# Revit family: HansWeitzel_4133
name_source: partatom
category: Allgemeines Modell
revit_build: Autodesk Revit 2017 (Build: 20160225_1515(x64)
units: mm (PartAtom-declared; Revit-internal decimal feet)

## family parameters
Basisbauteil = Wand
Beim Laden mit Abzugskörper schneiden = Nein
Bemaßung runder Anschluss = Durchmesser verwenden
Gemeinsam genutzt = Nein
Immer vertikal = Ja
Kann Basisbauteil für Bewehrung sein = Nein
Raumberechnungspunkt = Nein
Teiletyp = Normal

## types (1)
- HansWeitzel_4133
    BIM = https://media.live.bim.site
    BIMSITE_PRODUCT_ID = 6ce841d8c003c2f0351888f5bd4c5b56915332c2
    Beschreibung = HZ-Stoßverbinder BLF Buche dunkel Formteil an Sollbruchstelle einkürzen
    Breite [mm] = 40
    Dekor = Buche dunkel
    Farbton = Holzart/Holzdekor
    GTIN = 4022023208719
    Gewicht unverpackt (netto) [kg] = 0.008
    HAN = 4133
    HeinzeBIM = https://www.heinze.de
    Hersteller = Hans Weitzel GmbH & Co. KG
    Höhe [mm] = 93
    Ist System = Nein
    Ist Zubehör = Nein
    Menge pro Verpackungseinheit = 10
    Profilart = Anschlussprofi
    Tiefe (mm) = 30
    Typname = HZ-Stoßverbinder BLF Buche dunkel
    Wandmontage möglich = Ja
    Werkstoff = Polystyrol
    max. Betriebstemperatur (°C) = 90

## geometry (parser evidence)
native form markers: Sweep x5
no freeform markers — native parametric forms only
